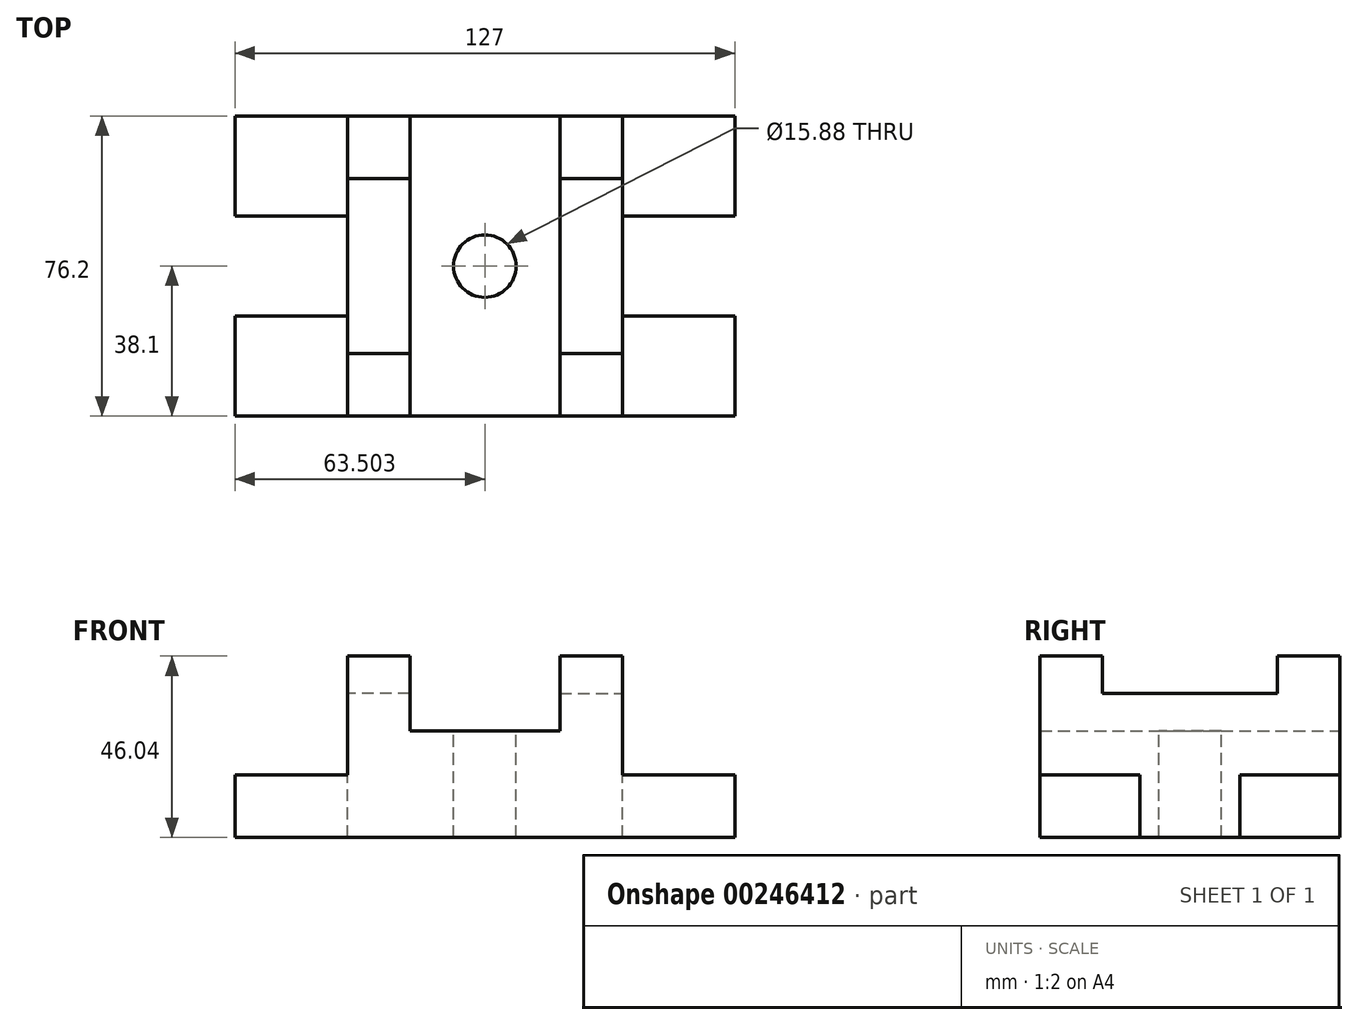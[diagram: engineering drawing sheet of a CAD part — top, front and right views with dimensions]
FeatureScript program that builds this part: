
annotation { "Feature Type Name" : "Feature", "Feature Type Description" : "" }
export const myFeature = defineFeature(function(context is Context, id is Id, definition is map)
    precondition{}
    {
        {
            var Q0;
            Q0=qCreatedBy(makeId("Front.planeOp"),FACE);
            var sketch = newSketch(context, id + "F0", { "sketchPlane" : qUnion([Q0])});
            skLineSegment(sketch, "E0.bottom", {"start": v(-66.88, -12.7) * mm, "end": v(-38.3, -12.7) * mm});
            skLineSegment(sketch, "E0.top", {"start": v(-66.88, -28.58) * mm, "end": v(60.12, -28.58) * mm});
            skLineSegment(sketch, "E0.left", {"start": v(-66.88, -12.7) * mm, "end": v(-66.88, -28.58) * mm});
            skLineSegment(sketch, "E0.right", {"start": v(60.12, -12.7) * mm, "end": v(60.12, -28.58) * mm});
            skLineSegment(sketch, "E1.top", {"start": v(-38.3, 17.46) * mm, "end": v(-22.43, 17.46) * mm});
            skLineSegment(sketch, "E1.left", {"start": v(-38.3, -12.7) * mm, "end": v(-38.3, 17.46) * mm});
            skLineSegment(sketch, "E1.right", {"start": v(-22.43, -1.6) * mm, "end": v(-22.43, 17.46) * mm});
            skLineSegment(sketch, "E2.top", {"start": v(15.67, 17.46) * mm, "end": v(31.55, 17.46) * mm});
            skLineSegment(sketch, "E2.left", {"start": v(15.67, -1.6) * mm, "end": v(15.67, 17.46) * mm});
            skLineSegment(sketch, "E2.right", {"start": v(31.55, -12.7) * mm, "end": v(31.55, 17.46) * mm});
            skLineSegment(sketch, "E3.trimOffspring", {"start": v(31.55, -12.7) * mm, "end": v(60.12, -12.7) * mm});
            skLineSegment(sketch, "E4.trimOffspring", {"start": v(-22.43, -1.6) * mm, "end": v(15.67, -1.6) * mm});
            skSolve(sketch);
        }
        {
            var Q0;
            Q0 = qSketchRegion(id + "F0", true);
            extrude(context, id + "F1", {"entities" : qUnion([Q0]), "endBound" : BoundingType.SYMMETRIC, "depth" : 76.2 * mm});
        }
        {
            var Q0;
            Q0=makeQuery(id+"F1.opExtrude","SWEPT_FACE",FACE,{"disambiguationData":[OSD([sQuery(id+"F0.wireOp",EDGE,"E0.left")])]});
            var sketch = newSketch(context, id + "F2", { "sketchPlane" : qUnion([Q0])});
            skLineSegment(sketch, "E5", {"start": v(12.7, -28.58) * mm, "end": v(12.7, -12.7) * mm});
            skLineSegment(sketch, "E6", {"start": v(12.7, -12.7) * mm, "end": v(-12.7, -12.7) * mm});
            skLineSegment(sketch, "E7", {"start": v(-12.7, -12.7) * mm, "end": v(-12.7, -12.7) * mm});
            skLineSegment(sketch, "E8", {"start": v(-12.7, -12.7) * mm, "end": v(-12.7, -28.58) * mm});
            skLineSegment(sketch, "E9", {"start": v(-12.7, -28.58) * mm, "end": v(12.7, -28.58) * mm});
            skLineSegment(sketch, "E10", {"start": v(-12.7, -28.58) * mm, "end": v(-38.1, -28.58) * mm});
            skLineSegment(sketch, "E11", {"start": v(12.7, -28.58) * mm, "end": v(38.1, -28.58) * mm});
            skSolve(sketch);
        }
        {
            var Q0;
            Q0 = qSketchRegion(id + "F2", true);
            var Q1;
            Q1=makeQuery(id+"F1.opExtrude","SWEPT_FACE",FACE,{"disambiguationData":[OSD([sQuery(id+"F0.wireOp",EDGE,"E1.left")])]});
            extrude(context, id + "F3", {"entities" : qUnion([Q0]), "operationType" : NewBodyOperationType.REMOVE, "endBound" : BoundingType.UP_TO_SURFACE, "oppositeDirection" : true, "endBoundEntityFace" : qUnion([Q1]), "depth" : 15.5 * mm});
        }
        {
            var Q0;
            Q0=makeQuery(id+"F1.opExtrude","SWEPT_FACE",FACE,{"disambiguationData":[OSD([sQuery(id+"F0.wireOp",EDGE,"E0.right")])]});
            var sketch = newSketch(context, id + "F4", { "sketchPlane" : qUnion([Q0])});
            skLineSegment(sketch, "E12", {"start": v(-12.7, -28.58) * mm, "end": v(-12.7, -12.7) * mm});
            skLineSegment(sketch, "E13", {"start": v(-12.7, -12.7) * mm, "end": v(12.7, -12.7) * mm});
            skLineSegment(sketch, "E14", {"start": v(12.7, -12.7) * mm, "end": v(12.7, -28.58) * mm});
            skLineSegment(sketch, "E15", {"start": v(-12.7, -28.58) * mm, "end": v(12.7, -28.58) * mm});
            skSolve(sketch);
        }
        {
            var Q0;
            Q0=makeQuery(id+"F4.imprint","IMPRINT",FACE,{"disambiguationData":[TD([[makeQuery(id+"F4.imprint","IMPRINT",EDGE,{"derivedFrom":sQuery(id+"F4.wireOp",EDGE,"E12")}),-1.0]])]});
            var Q1;
            Q1=makeQuery(id+"F1.opExtrude","SWEPT_FACE",FACE,{"disambiguationData":[OSD([sQuery(id+"F0.wireOp",EDGE,"E2.right")])]});
            extrude(context, id + "F5", {"entities" : qUnion([Q0]), "operationType" : NewBodyOperationType.REMOVE, "endBound" : BoundingType.UP_TO_SURFACE, "oppositeDirection" : true, "endBoundEntityFace" : qUnion([Q1]), "depth" : 25.4 * mm});
        }
        {
            var Q0;
            Q0=makeQuery(id+"F1.opExtrude","SWEPT_FACE",FACE,{"disambiguationData":[OSD([sQuery(id+"F0.wireOp",EDGE,"E4.trimOffspring")])]});
            var sketch = newSketch(context, id + "F6", { "sketchPlane" : qUnion([Q0])});
            skCircle(sketch, "E16", {"center": v(-3.38, 0) * mm, "radius": 7.94 * mm});
            skLineSegment(sketch, "E17", {"start": v(-22.43, 0) * mm, "end": v(15.67, 0) * mm});
            skSolve(sketch);
        }
        {
            var Q0;
            {var subQ0=sQuery(id+"F6.wireOp",EDGE,"E17");var subQ1=sQuery(id+"F6.wireOp",EDGE,"E16");var subQ2=makeQuery(id+"F6.imprint","INTERSECT",VERTEX,{"disambiguationData":[OD(0.0)],"derivedFrom":[subQ1,subQ0]});Q0=makeQuery(id+"F6.imprint","IMPRINT",FACE,{"disambiguationData":[TD([[makeQuery(id+"F6.imprint","IMPRINT",EDGE,{"disambiguationData":[TD([[subQ2,1.0]])],"derivedFrom":subQ1}),1.0]])]});}
            var Q1;
            {var subQ0=sQuery(id+"F6.wireOp",EDGE,"E17");var subQ1=sQuery(id+"F6.wireOp",EDGE,"E16");var subQ2=makeQuery(id+"F6.imprint","INTERSECT",VERTEX,{"disambiguationData":[OD(0.0)],"derivedFrom":[subQ1,subQ0]});Q1=makeQuery(id+"F6.imprint","IMPRINT",FACE,{"disambiguationData":[TD([[makeQuery(id+"F6.imprint","IMPRINT",EDGE,{"disambiguationData":[TD([[subQ2,-1.0]])],"derivedFrom":subQ1}),1.0]])]});}
            var Q2;
            Q2=sQuery(id+"F6.wireOp",EDGE,"E16");
            extrude(context, id + "F7", {"entities" : qUnion([Q0, Q1]), "operationType" : NewBodyOperationType.REMOVE, "surfaceEntities" : qUnion([Q2]), "oppositeDirection" : true, "depth" : 26.99 * mm});
        }
        {
            var Q0;
            {var subQ0=sQuery(id+"F0.wireOp",EDGE,"E2.right");Q0=makeQuery(id+"F5.boolean.opBoolean","MERGE",FACE,{"derivedFrom":[makeQuery(id+"F1.opExtrude","SWEPT_FACE",FACE,{"disambiguationData":[OSD([subQ0])]}),makeQuery(id+"F5.opExtrude","CAP_FACE",FACE,{"disambiguationData":[OSD([subQ0])],"isStart":false})]});}
            var sketch = newSketch(context, id + "F8", { "sketchPlane" : qUnion([Q0])});
            skLineSegment(sketch, "E18", {"start": v(-22.23, 17.46) * mm, "end": v(-22.23, 7.93) * mm});
            skLineSegment(sketch, "E19", {"start": v(22.23, 17.46) * mm, "end": v(22.23, 7.93) * mm});
            skLineSegment(sketch, "E20", {"start": v(-22.23, 7.93) * mm, "end": v(22.23, 7.93) * mm});
            skLineSegment(sketch, "E21", {"start": v(-22.23, 17.46) * mm, "end": v(22.23, 17.46) * mm});
            skSolve(sketch);
        }
        {
            var Q0;
            Q0=makeQuery(id+"F8.imprint","IMPRINT",FACE,{"disambiguationData":[TD([[makeQuery(id+"F8.imprint","IMPRINT",EDGE,{"derivedFrom":sQuery(id+"F8.wireOp",EDGE,"E18")}),1.0]])]});
            var Q1;
            Q1=makeQuery(id+"F1.opExtrude","SWEPT_FACE",FACE,{"disambiguationData":[OSD([sQuery(id+"F0.wireOp",EDGE,"E2.left")])]});
            extrude(context, id + "F9", {"entities" : qUnion([Q0]), "operationType" : NewBodyOperationType.REMOVE, "endBound" : BoundingType.UP_TO_SURFACE, "oppositeDirection" : true, "endBoundEntityFace" : qUnion([Q1]), "depth" : 11.68 * mm});
        }
        {
            var Q0;
            {var subQ0=sQuery(id+"F0.wireOp",EDGE,"E1.left");Q0=makeQuery(id+"F3.boolean.opBoolean","MERGE",FACE,{"derivedFrom":[makeQuery(id+"F1.opExtrude","SWEPT_FACE",FACE,{"disambiguationData":[OSD([subQ0])]}),makeQuery(id+"F3.opExtrude","CAP_FACE",FACE,{"disambiguationData":[OSD([subQ0])],"isStart":false})]});}
            var sketch = newSketch(context, id + "F10", { "sketchPlane" : qUnion([Q0])});
            skLineSegment(sketch, "E22", {"start": v(-38.1, 17.46) * mm, "end": v(-22.23, 17.46) * mm});
            skLineSegment(sketch, "E23", {"start": v(38.1, 17.46) * mm, "end": v(22.23, 17.46) * mm});
            skLineSegment(sketch, "E24", {"start": v(22.23, 17.46) * mm, "end": v(-22.23, 17.46) * mm});
            skLineSegment(sketch, "E25", {"start": v(-22.23, 17.46) * mm, "end": v(-22.23, 7.93) * mm});
            skLineSegment(sketch, "E26", {"start": v(-22.23, 7.93) * mm, "end": v(22.23, 7.93) * mm});
            skLineSegment(sketch, "E27", {"start": v(22.23, 7.93) * mm, "end": v(22.23, 17.46) * mm});
            skSolve(sketch);
        }
        {
            var Q0;
            Q0=makeQuery(id+"F10.imprint","IMPRINT",FACE,{"disambiguationData":[TD([[makeQuery(id+"F10.imprint","IMPRINT",EDGE,{"derivedFrom":sQuery(id+"F10.wireOp",EDGE,"E24")}),1.0]])]});
            var Q1;
            Q1=qCreatedBy(makeId("Right.planeOp"),FACE);
            extrude(context, id + "F11", {"entities" : qUnion([Q0]), "operationType" : NewBodyOperationType.REMOVE, "endBound" : BoundingType.UP_TO_SURFACE, "oppositeDirection" : true, "endBoundEntityFace" : qUnion([Q1]), "depth" : 25.4 * mm});
        }
    });
